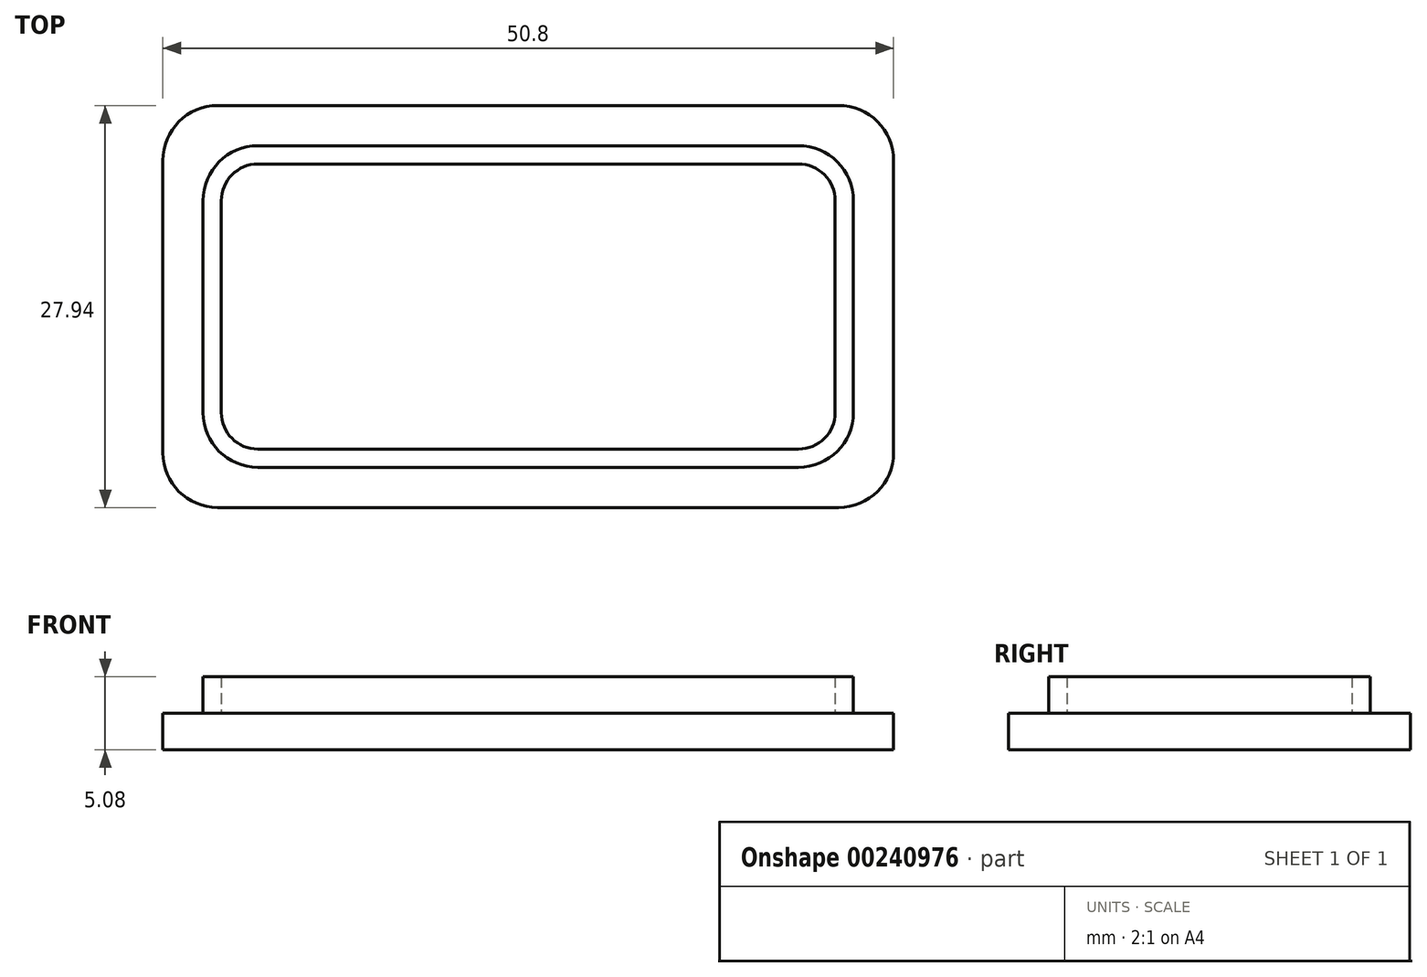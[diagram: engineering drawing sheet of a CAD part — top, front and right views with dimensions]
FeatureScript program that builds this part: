
annotation { "Feature Type Name" : "Feature", "Feature Type Description" : "" }
export const myFeature = defineFeature(function(context is Context, id is Id, definition is map)
    precondition{}
    {
        {
            var Q0;
            Q0=qCreatedBy(makeId("Top.planeOp"),FACE);
            var sketch = newSketch(context, id + "F0", { "sketchPlane" : qUnion([Q0])});
            skLineSegment(sketch, "E0.bottom", {"start": v(25.4, -13.97) * mm, "end": v(-25.4, -13.97) * mm});
            skLineSegment(sketch, "E0.top", {"start": v(25.4, 13.97) * mm, "end": v(-25.4, 13.97) * mm});
            skLineSegment(sketch, "E0.left", {"start": v(25.4, -13.97) * mm, "end": v(25.4, 13.97) * mm});
            skLineSegment(sketch, "E0.right", {"start": v(-25.4, -13.97) * mm, "end": v(-25.4, 13.97) * mm});
            skPoint(sketch, "E0.middle", {"position": v(0, 0) * mm});
            skSolve(sketch);
        }
        {
            var Q0;
            Q0 = qSketchRegion(id + "F0", true);
            extrude(context, id + "F1", {"entities" : qUnion([Q0]), "depth" : 2.54 * mm});
        }
        {
            var Q0;
            Q0=makeQuery(id+"F1.opExtrude","SWEPT_EDGE",EDGE,{"disambiguationData":[OSD([sQuery(id+"F0.wireOp",EDGE,"E0.top"),sQuery(id+"F0.wireOp",EDGE,"E0.right")])]});
            var Q1;
            Q1=makeQuery(id+"F1.opExtrude","SWEPT_EDGE",EDGE,{"disambiguationData":[OSD([sQuery(id+"F0.wireOp",EDGE,"E0.top"),sQuery(id+"F0.wireOp",EDGE,"E0.left")])]});
            var Q2;
            Q2=makeQuery(id+"F1.opExtrude","SWEPT_EDGE",EDGE,{"disambiguationData":[OSD([sQuery(id+"F0.wireOp",EDGE,"E0.bottom"),sQuery(id+"F0.wireOp",EDGE,"E0.right")])]});
            var Q3;
            Q3=makeQuery(id+"F1.opExtrude","SWEPT_EDGE",EDGE,{"disambiguationData":[OSD([sQuery(id+"F0.wireOp",EDGE,"E0.bottom"),sQuery(id+"F0.wireOp",EDGE,"E0.left")])]});
            fillet(context, id + "F2", {"entities" : qUnion([Q0, Q1, Q2, Q3]), "radius" : 3.8 * mm, "tangentPropagation" : true, "allowEdgeOverflow" : false});
        }
        {
            var Q0;
            Q0=makeQuery(id+"F1.opExtrude","CAP_FACE",FACE,{"disambiguationData":[OSD([sQuery(id+"F0.wireOp",EDGE,"E0.bottom"),sQuery(id+"F0.wireOp",EDGE,"E0.top"),sQuery(id+"F0.wireOp",EDGE,"E0.left"),sQuery(id+"F0.wireOp",EDGE,"E0.right")])],"isStart":false});
            var sketch = newSketch(context, id + "F3", { "sketchPlane" : qUnion([Q0])});
            skLineSegment(sketch, "E1.bottom", {"start": v(18.8, -11.18) * mm, "end": v(-18.8, -11.18) * mm});
            skLineSegment(sketch, "E1.top", {"start": v(18.8, 11.18) * mm, "end": v(-18.8, 11.18) * mm});
            skLineSegment(sketch, "E1.left", {"start": v(22.6, -7.37) * mm, "end": v(22.6, 7.37) * mm});
            skLineSegment(sketch, "E1.right", {"start": v(-22.6, -7.37) * mm, "end": v(-22.6, 7.37) * mm});
            skPoint(sketch, "E1.middle", {"position": v(0, 0) * mm});
            skPoint(sketch, "E2.visualSharp", {"position": v(-22.6, 11.18) * mm});
            skArc(sketch, "E2.filletArc", {"start": v(-18.8, 11.18) * mm, "mid": v(-21.5, 10.06) * mm, "end": v(-22.6, 7.37) * mm});
            skPoint(sketch, "E3.visualSharp", {"position": v(22.6, 11.18) * mm});
            skArc(sketch, "E3.filletArc", {"start": v(22.6, 7.37) * mm, "mid": v(21.5, 10.06) * mm, "end": v(18.8, 11.18) * mm});
            skPoint(sketch, "E4.visualSharp", {"position": v(22.6, -11.18) * mm});
            skArc(sketch, "E4.filletArc", {"start": v(18.8, -11.18) * mm, "mid": v(21.5, -10.06) * mm, "end": v(22.6, -7.37) * mm});
            skPoint(sketch, "E5.visualSharp", {"position": v(-22.6, -11.18) * mm});
            skArc(sketch, "E5.filletArc", {"start": v(-22.6, -7.37) * mm, "mid": v(-21.5, -10.06) * mm, "end": v(-18.8, -11.18) * mm});
            skArc(sketch, "E6.0", {"start": v(21.34, 7.37) * mm, "mid": v(20.6, 9.16) * mm, "end": v(18.8, 9.9) * mm});
            skLineSegment(sketch, "E6.1", {"start": v(21.34, -7.37) * mm, "end": v(21.34, 7.37) * mm});
            skLineSegment(sketch, "E6.2", {"start": v(18.8, 9.9) * mm, "end": v(-18.8, 9.9) * mm});
            skArc(sketch, "E6.3", {"start": v(18.8, -9.9) * mm, "mid": v(20.6, -9.16) * mm, "end": v(21.34, -7.37) * mm});
            skArc(sketch, "E6.4", {"start": v(-18.8, 9.9) * mm, "mid": v(-20.6, 9.16) * mm, "end": v(-21.34, 7.37) * mm});
            skLineSegment(sketch, "E6.5", {"start": v(-21.34, -7.37) * mm, "end": v(-21.34, 7.37) * mm});
            skArc(sketch, "E6.6", {"start": v(-21.34, -7.37) * mm, "mid": v(-20.6, -9.16) * mm, "end": v(-18.8, -9.9) * mm});
            skLineSegment(sketch, "E6.7", {"start": v(18.8, -9.9) * mm, "end": v(-18.8, -9.9) * mm});
            skSolve(sketch);
        }
        {
            var Q0;
            Q0=makeQuery(id+"F3.imprint","IMPRINT",FACE,{"disambiguationData":[TD([[makeQuery(id+"F3.imprint","IMPRINT",EDGE,{"derivedFrom":sQuery(id+"F3.wireOp",EDGE,"E1.bottom")}),-1.0]])]});
            extrude(context, id + "F4", {"entities" : qUnion([Q0]), "operationType" : NewBodyOperationType.ADD, "depth" : 2.54 * mm});
        }
    });
